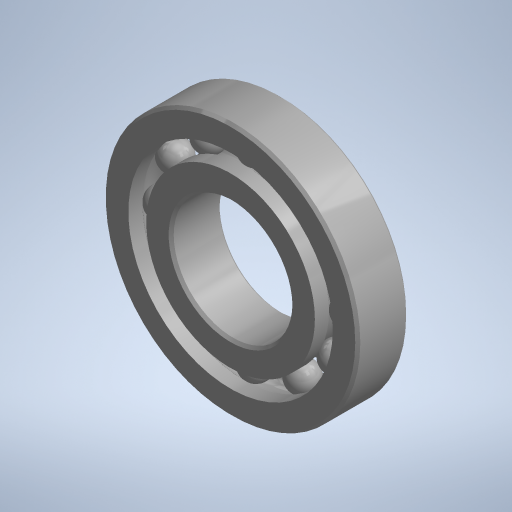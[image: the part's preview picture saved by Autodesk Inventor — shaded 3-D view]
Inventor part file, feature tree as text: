
AUTODESK INVENTOR PART (.ipt)
format: ipt  version: 2023.4 (Build 274418000, 418)  size: 629,248 bytes
history: mixed  units: mm (DEFAULTED — no unit token found)
features: other x11, revolve x3, imported_body x1
ambient origin geometry x8: Origin, YZ Plane, XZ Plane, XY Plane, X Axis, Y Axis, Z Axis, Center Point
bodies: Solid1 (imported_parasolid), Solid2 (imported_parasolid), Solid3 (imported_parasolid), Solid4 (imported_parasolid), Solid5 (imported_parasolid), Solid6 (imported_parasolid), Solid7 (imported_parasolid), Solid8 (imported_parasolid), Solid9 (imported_parasolid), Solid10 (imported_parasolid), Solid11 (imported_parasolid), Solid12 (imported_parasolid), Solid13 (imported_parasolid), Solid14 (imported_parasolid)
feature tree (15):
  revolve  "Revolve1"  [1 undecoded]
  revolve  "Revolve3"  [1 undecoded]
  revolve  "Revolve4"  [1 undecoded]
  other  "CirPattern1[1]"
  other  "CirPattern1[2]"
  other  "CirPattern1[3]"
  other  "CirPattern1[4]"
  other  "CirPattern1[5]"
  other  "CirPattern1[6]"
  other  "CirPattern1[7]"
  other  "CirPattern1[8]"
  other  "CirPattern1[9]"
  other  "CirPattern1[10]"
  other  "CirPattern1[11]"
  imported_body  NMx_Import_Brep_tag  [imported B-rep: ~28 faces, bbox_mm=[12.7, 0.0, 9.525]]
note: 3 required parameter values undecoded (feature->parameter linkage not recoverable at this tier; creation-order binding heuristic only, values carry confidence <= 0.55)
